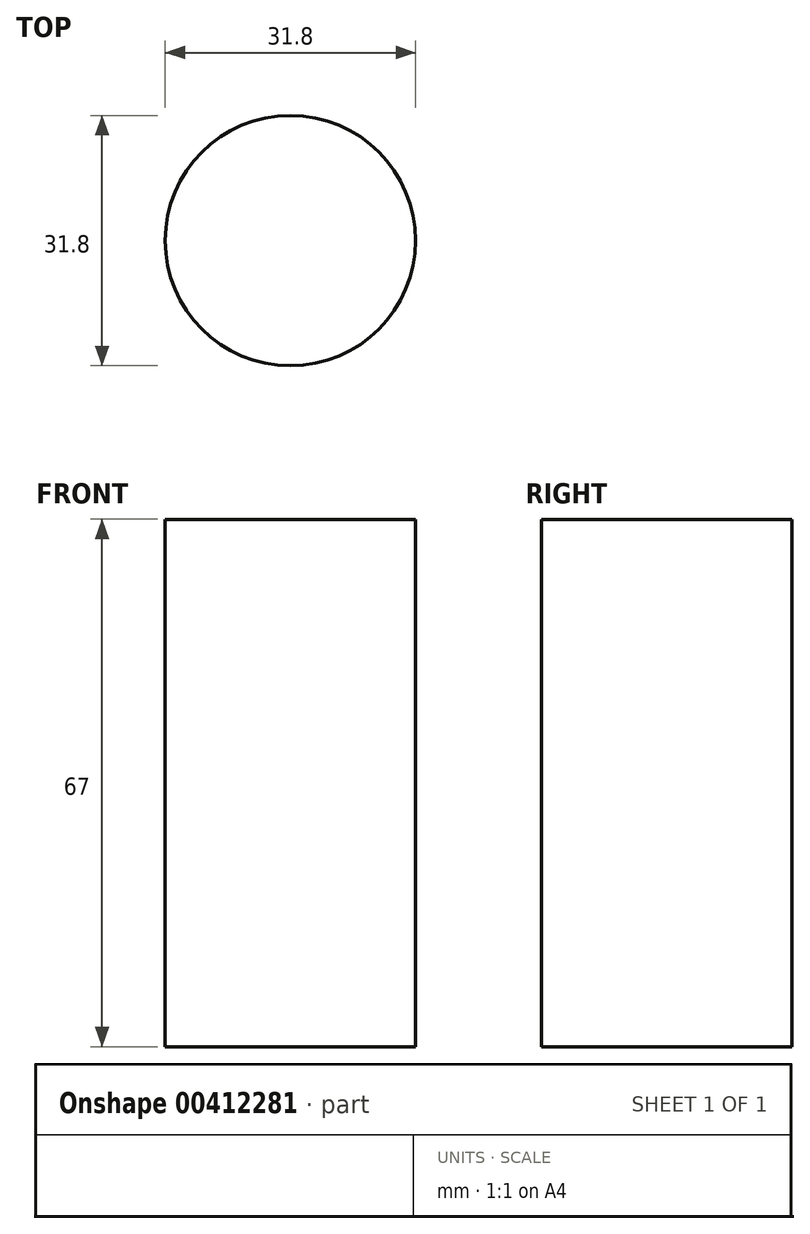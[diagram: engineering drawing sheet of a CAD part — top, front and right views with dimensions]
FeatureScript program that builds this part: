
annotation { "Feature Type Name" : "Feature", "Feature Type Description" : "" }
export const myFeature = defineFeature(function(context is Context, id is Id, definition is map)
    precondition{}
    {
        {
            var Q0;
            Q0=qCreatedBy(makeId("Front.planeOp"),FACE);
            var sketch = newSketch(context, id + "F0", { "sketchPlane" : qUnion([Q0])});
            skLineSegment(sketch, "E0", {"start": v(0, 0) * mm, "end": v(-15.9, 0) * mm});
            skLineSegment(sketch, "E1", {"start": v(-15.9, 0) * mm, "end": v(-15.9, 67) * mm});
            skLineSegment(sketch, "E2", {"start": v(-15.9, 67) * mm, "end": v(0, 67) * mm});
            skLineSegment(sketch, "E3", {"start": v(0, 0) * mm, "end": v(0, 67) * mm});
            skSolve(sketch);
        }
        {
            var Q0;
            Q0=makeQuery(id+"F0.imprint","IMPRINT",FACE,{"disambiguationData":[TD([[makeQuery(id+"F0.imprint","IMPRINT",EDGE,{"derivedFrom":sQuery(id+"F0.wireOp",EDGE,"E0")}),-1.0]])]});
            var Q1;
            Q1=sQuery(id+"F0.wireOp",EDGE,"E3");
            revolve(context, id + "F1", {"entities" : qUnion([Q0]), "axis" : qUnion([Q1]), "revolveType" : RevolveType.FULL});
        }
    });
